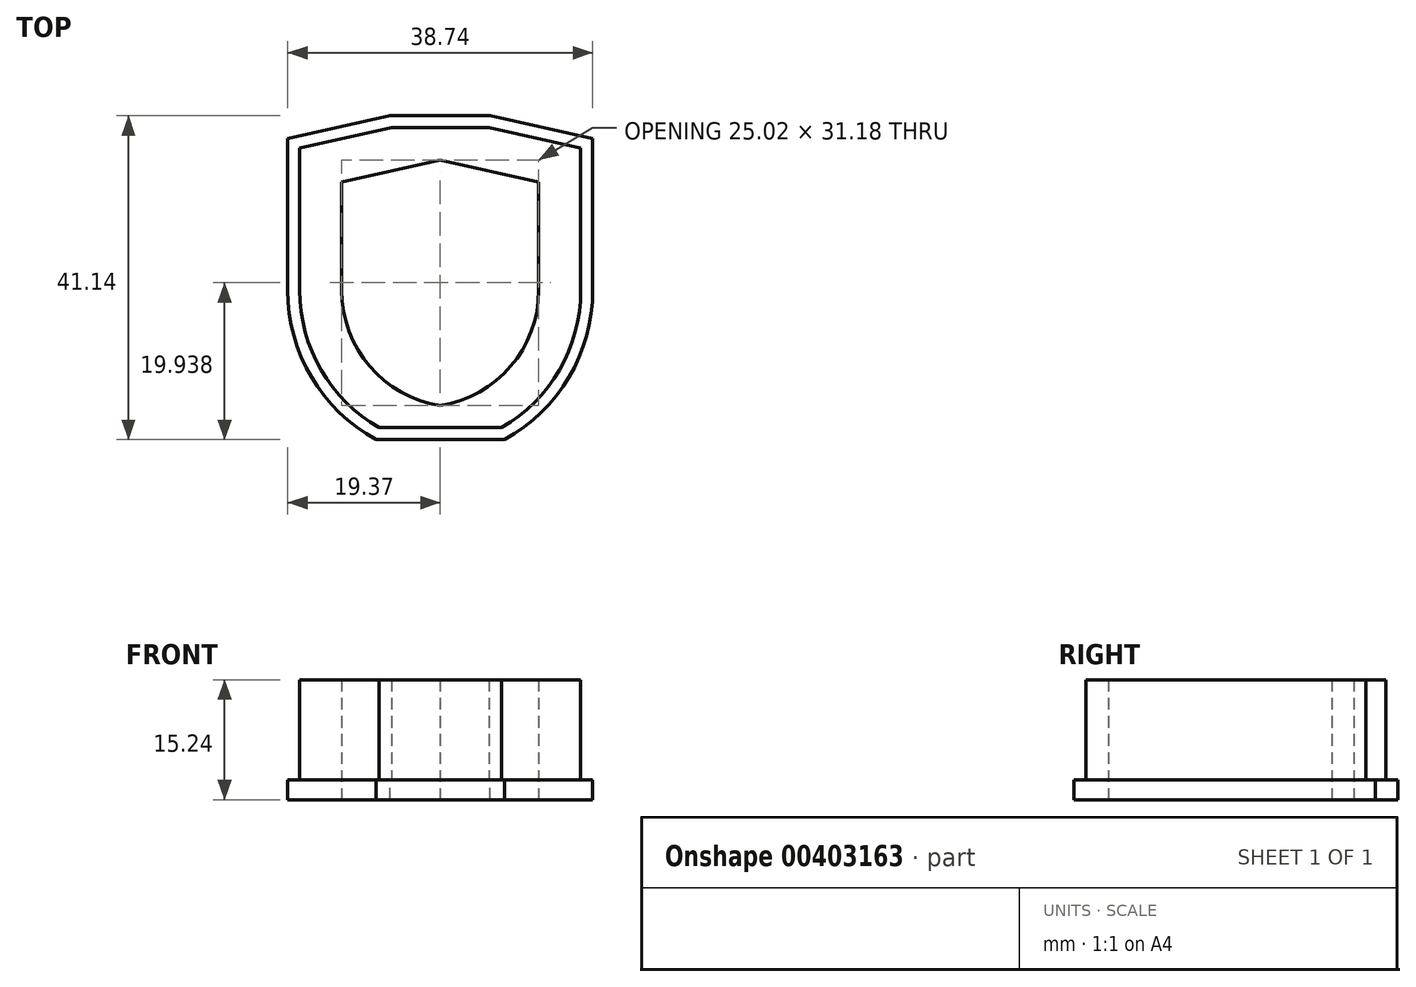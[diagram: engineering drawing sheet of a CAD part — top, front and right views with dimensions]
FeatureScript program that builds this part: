
annotation { "Feature Type Name" : "Feature", "Feature Type Description" : "" }
export const myFeature = defineFeature(function(context is Context, id is Id, definition is map)
    precondition{}
    {
        {
            var Q0;
            Q0=qCreatedBy(makeId("Top.planeOp"),FACE);
            var sketch = newSketch(context, id + "F0", { "sketchPlane" : qUnion([Q0])});
            skLineSegment(sketch, "E0.left", {"start": v(-14.29, 14.22) * mm, "end": v(-14.29, -1.02) * mm});
            skLineSegment(sketch, "E0.right", {"start": v(14.29, 14.22) * mm, "end": v(14.29, -1.02) * mm});
            skLineSegment(sketch, "E1", {"start": v(0, 17.4) * mm, "end": v(14.29, 14.22) * mm});
            skArc(sketch, "E2", {"start": v(0, -17.4) * mm, "mid": v(10.21, -11.88) * mm, "end": v(14.29, -1.02) * mm});
            skLineSegment(sketch, "E3.MirrorCS", {"start": v(0, 17.4) * mm, "end": v(-14.29, 14.22) * mm});
            skArc(sketch, "E4.MirrorCS", {"start": v(0, -17.4) * mm, "mid": v(-10.21, -11.88) * mm, "end": v(-14.29, -1.02) * mm});
            skPoint(sketch, "E0.bottom.start.orphan", {"position": v(-14.29, 17.4) * mm});
            skPoint(sketch, "E5.orphan", {"position": v(-14.29, -17.4) * mm});
            skPoint(sketch, "E6.orphan", {"position": v(14.29, -17.4) * mm});
            skPoint(sketch, "E7.orphan", {"position": v(14.29, 17.4) * mm});
            skLineSegment(sketch, "E8.0", {"start": v(-10.16, 15.92) * mm, "end": v(-15.05, 14.84) * mm});
            skLineSegment(sketch, "E8.1", {"start": v(15.05, 14.84) * mm, "end": v(15.05, -1.02) * mm});
            skArc(sketch, "E8.2", {"start": v(10.16, -13.07) * mm, "mid": v(13.78, -7.52) * mm, "end": v(15.05, -1.02) * mm});
            skLineSegment(sketch, "E8.3", {"start": v(10.16, 15.92) * mm, "end": v(15.05, 14.84) * mm});
            skArc(sketch, "E8.4", {"start": v(-10.16, -13.07) * mm, "mid": v(-13.78, -7.52) * mm, "end": v(-15.05, -1.02) * mm});
            skLineSegment(sketch, "E8.5", {"start": v(-15.05, 14.84) * mm, "end": v(-15.05, -1.02) * mm});
            skLineSegment(sketch, "E9", {"start": v(-10.16, 19.17) * mm, "end": v(-10.16, 15.92) * mm});
            skLineSegment(sketch, "E10.MirrorCS", {"start": v(10.16, 19.17) * mm, "end": v(10.16, 15.92) * mm});
            skLineSegment(sketch, "E11.0", {"start": v(10.16, 19.17) * mm, "end": v(18.22, 17.38) * mm});
            skLineSegment(sketch, "E11.1", {"start": v(-18.22, 17.38) * mm, "end": v(-18.22, -1.02) * mm});
            skArc(sketch, "E11.2", {"start": v(-10.16, -17.3) * mm, "mid": v(-16.1, -10.1) * mm, "end": v(-18.22, -1.02) * mm});
            skLineSegment(sketch, "E11.3", {"start": v(-10.16, 19.17) * mm, "end": v(-18.22, 17.38) * mm});
            skArc(sketch, "E11.4", {"start": v(10.16, -17.3) * mm, "mid": v(16.1, -10.1) * mm, "end": v(18.22, -1.02) * mm});
            skLineSegment(sketch, "E11.5", {"start": v(18.22, 17.38) * mm, "end": v(18.22, -1.02) * mm});
            skPoint(sketch, "E12.orphan", {"position": v(-10.16, 22.27) * mm});
            skLineSegment(sketch, "E13.trimOffspring", {"start": v(-10.16, -13.07) * mm, "end": v(-10.16, -17.3) * mm});
            skLineSegment(sketch, "E14.trimOffspring", {"start": v(10.16, -13.07) * mm, "end": v(10.16, -17.3) * mm});
            skPoint(sketch, "E15.orphan", {"position": v(10.16, 22.27) * mm});
            skPoint(sketch, "E16.orphan", {"position": v(10.16, -23.7) * mm});
            skPoint(sketch, "E17.orphan", {"position": v(-10.16, -23.7) * mm});
            skSolve(sketch);
        }
        {
            var Q0;
            Q0=qCreatedBy(makeId("Top.planeOp"),FACE);
            var sketch = newSketch(context, id + "F1", { "sketchPlane" : qUnion([Q0])});
            skArc(sketch, "E18.0", {"start": v(-7.77, -18.43) * mm, "mid": v(-15.15, -11.07) * mm, "end": v(-17.84, -1.02) * mm});
            skLineSegment(sketch, "E18.1", {"start": v(-17.84, 17.08) * mm, "end": v(-17.84, -1.02) * mm});
            skLineSegment(sketch, "E18.2", {"start": v(-6.17, 19.67) * mm, "end": v(-17.84, 17.08) * mm});
            skArc(sketch, "E19.MirrorCS", {"start": v(7.77, -18.43) * mm, "mid": v(15.15, -11.07) * mm, "end": v(17.84, -1.02) * mm});
            skLineSegment(sketch, "E20.MirrorCS", {"start": v(6.17, 19.67) * mm, "end": v(17.84, 17.08) * mm});
            skLineSegment(sketch, "E21.MirrorCS", {"start": v(17.84, 17.08) * mm, "end": v(17.84, -1.02) * mm});
            skLineSegment(sketch, "E22", {"start": v(-6.17, 19.67) * mm, "end": v(6.17, 19.67) * mm});
            skLineSegment(sketch, "E23", {"start": v(-7.77, -18.43) * mm, "end": v(7.77, -18.43) * mm});
            skLineSegment(sketch, "E24.0", {"start": v(-6.34, 21.2) * mm, "end": v(-19.37, 18.3) * mm});
            skLineSegment(sketch, "E24.1", {"start": v(-19.37, 18.3) * mm, "end": v(-19.37, -1.02) * mm});
            skLineSegment(sketch, "E24.2", {"start": v(-6.34, 21.2) * mm, "end": v(6.34, 21.2) * mm});
            skArc(sketch, "E24.3", {"start": v(-8.17, -19.95) * mm, "mid": v(-16.36, -12.02) * mm, "end": v(-19.37, -1.02) * mm});
            skLineSegment(sketch, "E24.4", {"start": v(6.34, 21.2) * mm, "end": v(19.37, 18.3) * mm});
            skLineSegment(sketch, "E24.5", {"start": v(19.37, 18.3) * mm, "end": v(19.37, -1.02) * mm});
            skArc(sketch, "E24.6", {"start": v(8.17, -19.95) * mm, "mid": v(16.36, -12.02) * mm, "end": v(19.37, -1.02) * mm});
            skLineSegment(sketch, "E24.7", {"start": v(-8.17, -19.95) * mm, "end": v(8.17, -19.95) * mm});
            skLineSegment(sketch, "E25.0", {"start": v(0, 15.58) * mm, "end": v(12.5, 12.8) * mm});
            skLineSegment(sketch, "E25.1", {"start": v(-12.5, 12.8) * mm, "end": v(-12.5, -1.02) * mm});
            skArc(sketch, "E25.2", {"start": v(0, -15.6) * mm, "mid": v(-8.95, -10.62) * mm, "end": v(-12.5, -1.02) * mm});
            skLineSegment(sketch, "E25.3", {"start": v(0, 15.58) * mm, "end": v(-12.5, 12.8) * mm});
            skArc(sketch, "E25.4", {"start": v(0, -15.6) * mm, "mid": v(8.95, -10.62) * mm, "end": v(12.5, -1.02) * mm});
            skLineSegment(sketch, "E25.5", {"start": v(12.5, 12.8) * mm, "end": v(12.5, -1.02) * mm});
            skSolve(sketch);
        }
        {
            var Q0;
            Q0=makeQuery(id+"F1.imprint","IMPRINT",FACE,{"disambiguationData":[TD([[makeQuery(id+"F1.imprint","IMPRINT",EDGE,{"derivedFrom":sQuery(id+"F1.wireOp",EDGE,"E18.0")}),1.0]])]});
            extrude(context, id + "F2", {"entities" : qUnion([Q0]), "depth" : 12.7 * mm});
        }
        {
            var Q0;
            Q0=makeQuery(id+"F2.opExtrude","CAP_FACE",FACE,{"disambiguationData":[OSD([sQuery(id+"F1.wireOp",EDGE,"E18.0"),sQuery(id+"F1.wireOp",EDGE,"E18.1"),sQuery(id+"F1.wireOp",EDGE,"E18.2"),sQuery(id+"F1.wireOp",EDGE,"E19.MirrorCS"),sQuery(id+"F1.wireOp",EDGE,"E20.MirrorCS"),sQuery(id+"F1.wireOp",EDGE,"E21.MirrorCS"),sQuery(id+"F1.wireOp",EDGE,"E22"),sQuery(id+"F1.wireOp",EDGE,"E23"),sQuery(id+"F1.wireOp",EDGE,"E24.0"),sQuery(id+"F1.wireOp",EDGE,"E24.1"),sQuery(id+"F1.wireOp",EDGE,"E24.2"),sQuery(id+"F1.wireOp",EDGE,"E24.3"),sQuery(id+"F1.wireOp",EDGE,"E24.4"),sQuery(id+"F1.wireOp",EDGE,"E24.5"),sQuery(id+"F1.wireOp",EDGE,"E24.6"),sQuery(id+"F1.wireOp",EDGE,"E24.7")])],"isStart":true});
            var sketch = newSketch(context, id + "F3", { "sketchPlane" : qUnion([Q0])});
            skArc(sketch, "E26.0", {"start": v(-8.17, 19.95) * mm, "mid": v(-16.36, 12.02) * mm, "end": v(-19.37, 1.02) * mm});
            skLineSegment(sketch, "E27.0", {"start": v(-8.17, 19.95) * mm, "end": v(8.17, 19.95) * mm});
            skArc(sketch, "E28.0", {"start": v(8.17, 19.95) * mm, "mid": v(16.36, 12.02) * mm, "end": v(19.37, 1.02) * mm});
            skLineSegment(sketch, "E29.0", {"start": v(19.37, -18.3) * mm, "end": v(19.37, 1.02) * mm});
            skLineSegment(sketch, "E30.0", {"start": v(6.34, -21.2) * mm, "end": v(19.37, -18.3) * mm});
            skLineSegment(sketch, "E31.0", {"start": v(-6.34, -21.2) * mm, "end": v(6.34, -21.2) * mm});
            skLineSegment(sketch, "E32.0", {"start": v(-6.34, -21.2) * mm, "end": v(-19.37, -18.3) * mm});
            skLineSegment(sketch, "E33.0", {"start": v(-19.37, -18.3) * mm, "end": v(-19.37, 1.02) * mm});
            skSolve(sketch);
        }
        {
            var Q0;
            Q0 = qSketchRegion(id + "F3", true);
            extrude(context, id + "F4", {"entities" : qUnion([Q0]), "operationType" : NewBodyOperationType.ADD, "depth" : 2.54 * mm});
        }
        {
            var Q0;
            Q0=makeQuery(id+"F1.imprint","IMPRINT",FACE,{"disambiguationData":[TD([[makeQuery(id+"F1.imprint","IMPRINT",EDGE,{"derivedFrom":sQuery(id+"F1.wireOp",EDGE,"E25.0")}),-1.0]])]});
            extrude(context, id + "F5", {"entities" : qUnion([Q0]), "operationType" : NewBodyOperationType.REMOVE, "oppositeDirection" : true, "depth" : 25.4 * mm});
        }
    });
